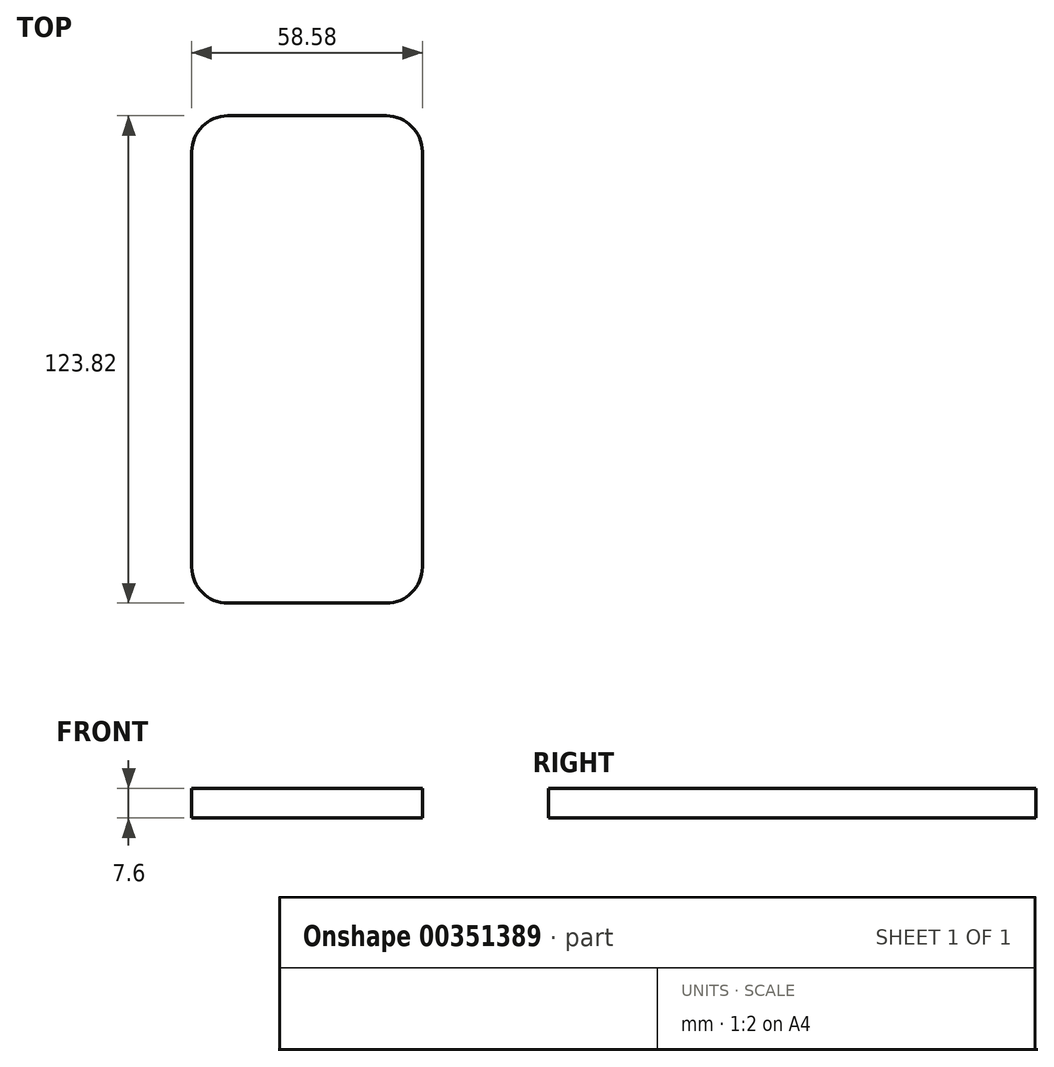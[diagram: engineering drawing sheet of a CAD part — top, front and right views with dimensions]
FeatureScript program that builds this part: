
annotation { "Feature Type Name" : "Feature", "Feature Type Description" : "" }
export const myFeature = defineFeature(function(context is Context, id is Id, definition is map)
    precondition{}
    {
        {
            var Q0;
            Q0=qCreatedBy(makeId("Top.planeOp"),FACE);
            var sketch = newSketch(context, id + "F0", { "sketchPlane" : qUnion([Q0])});
            skLineSegment(sketch, "E0.bottom", {"start": v(20.13, 61.92) * mm, "end": v(-20.14, 61.92) * mm});
            skLineSegment(sketch, "E0.top", {"start": v(20.14, -61.91) * mm, "end": v(-20.13, -61.91) * mm});
            skLineSegment(sketch, "E0.left", {"start": v(29.29, 52.77) * mm, "end": v(29.28, -52.77) * mm});
            skLineSegment(sketch, "E0.right", {"start": v(-29.29, 52.77) * mm, "end": v(-29.28, -52.77) * mm});
            skPoint(sketch, "E0.middle", {"position": v(0, 0) * mm});
            skPoint(sketch, "E1.visualSharp", {"position": v(29.29, 61.92) * mm});
            skArc(sketch, "E1.filletArc", {"start": v(29.29, 52.77) * mm, "mid": v(26.6, 59.24) * mm, "end": v(20.13, 61.92) * mm});
            skPoint(sketch, "E2.visualSharp", {"position": v(-29.29, 61.92) * mm});
            skArc(sketch, "E2.filletArc", {"start": v(-20.14, 61.92) * mm, "mid": v(-26.6, 59.24) * mm, "end": v(-29.29, 52.77) * mm});
            skPoint(sketch, "E3.visualSharp", {"position": v(29.29, -61.91) * mm});
            skArc(sketch, "E3.filletArc", {"start": v(20.14, -61.91) * mm, "mid": v(26.6, -59.24) * mm, "end": v(29.29, -52.77) * mm});
            skPoint(sketch, "E4.visualSharp", {"position": v(-29.28, -61.91) * mm});
            skArc(sketch, "E4.filletArc", {"start": v(-29.29, -52.77) * mm, "mid": v(-26.6, -59.24) * mm, "end": v(-20.13, -61.91) * mm});
            skLineSegment(sketch, "E5", {"start": v(29.29, -50.31) * mm, "end": v(-29.28, -50.31) * mm});
            skLineSegment(sketch, "E6", {"start": v(29.28, -61.91) * mm, "end": v(29.28, -50.91) * mm});
            skLineSegment(sketch, "E7", {"start": v(29.29, -50.91) * mm, "end": v(-29.28, -50.92) * mm});
            skLineSegment(sketch, "E8", {"start": v(29.28, 50.92) * mm, "end": v(-29.29, 50.92) * mm});
            skLineSegment(sketch, "E9", {"start": v(29.28, 61.92) * mm, "end": v(29.29, 50.32) * mm});
            skLineSegment(sketch, "E10", {"start": v(29.29, 50.32) * mm, "end": v(-29.29, 50.31) * mm});
            skSolve(sketch);
        }
        {
            var Q0;
            Q0 = qSketchRegion(id + "F0", true);
            extrude(context, id + "F1", {"entities" : qUnion([Q0]), "depth" : 7.6 * mm});
        }
    });
